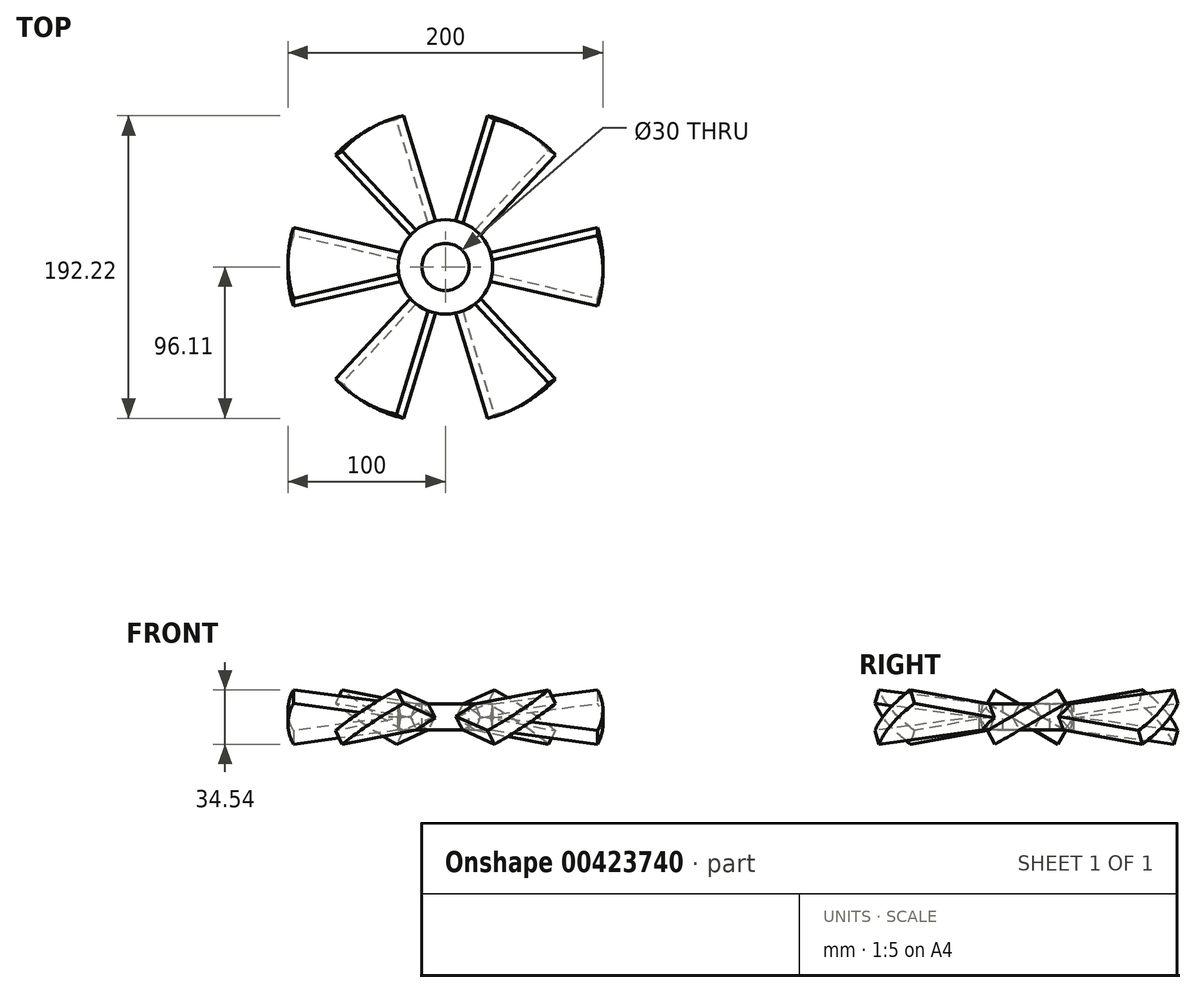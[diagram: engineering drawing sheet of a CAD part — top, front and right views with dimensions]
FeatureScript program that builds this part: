
annotation { "Feature Type Name" : "Feature", "Feature Type Description" : "" }
export const myFeature = defineFeature(function(context is Context, id is Id, definition is map)
    precondition{}
    {
        {
            var Q0;
            Q0=qCreatedBy(makeId("Top.planeOp"),FACE);
            var sketch = newSketch(context, id + "F0", { "sketchPlane" : qUnion([Q0])});
            skCircle(sketch, "E0", {"center": v(0, 0) * mm, "radius": 100 * mm});
            skCircle(sketch, "E1", {"center": v(0, 0) * mm, "radius": 30 * mm});
            skCircle(sketch, "E2", {"center": v(0, 0) * mm, "radius": 15 * mm});
            skLineSegment(sketch, "E3", {"start": v(0, 0) * mm, "end": v(15, 0) * mm});
            skLineSegment(sketch, "E4", {"start": v(14.49, 3.88) * mm, "end": v(96.6, 25.88) * mm});
            skLineSegment(sketch, "E5.MirrorCS", {"start": v(14.49, -3.88) * mm, "end": v(96.6, -25.88) * mm});
            skLineSegment(sketch, "E6", {"start": v(14.49, 3.88) * mm, "end": v(0, 0) * mm});
            skLineSegment(sketch, "E7", {"start": v(0, 0) * mm, "end": v(14.49, -3.88) * mm});
            skSolve(sketch);
        }
        {
            var Q0;
            {var subQ0=sQuery(id+"F0.wireOp",EDGE,"E4");var subQ1=sQuery(id+"F0.wireOp",EDGE,"E0");var subQ2=makeQuery(id+"F0.imprint","INTERSECT",VERTEX,{"derivedFrom":[subQ1,subQ0]});Q0=makeQuery(id+"F0.imprint","IMPRINT",FACE,{"disambiguationData":[TD([[makeQuery(id+"F0.imprint","IMPRINT",EDGE,{"disambiguationData":[TD([[subQ2,1.0]])],"derivedFrom":subQ1}),1.0]])]});}
            var Q1;
            {var subQ4=sQuery(id+"F0.wireOp",EDGE,"E4");var subQ6=sQuery(id+"F0.wireOp",EDGE,"E1");var subQ7=makeQuery(id+"F0.imprint","INTERSECT",VERTEX,{"derivedFrom":[subQ6,subQ4]});Q1=makeQuery(id+"F0.imprint","IMPRINT",FACE,{"disambiguationData":[TD([[makeQuery(id+"F0.imprint","IMPRINT",EDGE,{"disambiguationData":[TD([[subQ7,1.0]])],"derivedFrom":subQ6}),1.0]])]});}
            extrude(context, id + "F1", {"entities" : qUnion([Q0, Q1]), "endBound" : BoundingType.SYMMETRIC, "depth" : 10 * mm});
        }
        {
            var Q0;
            Q0=makeQuery(id+"F1.opExtrude","SWEPT_BODY",BODY,{"disambiguationData":[OSD([sQuery(id+"F0.wireOp",EDGE,"E0"),sQuery(id+"F0.wireOp",EDGE,"E2"),sQuery(id+"F0.wireOp",EDGE,"E4"),sQuery(id+"F0.wireOp",EDGE,"E5.MirrorCS")])]});
            var Q1;
            Q1=sQuery(id+"F0.wireOp",EDGE,"E3");
            var Q2;
            Q2=sQuery(id+"F0.wireOp",EDGE,"E3");
            transform(context, id + "F2", {"entities" : qUnion([Q0]), "transformType" : TransformType.ROTATION, "transformAxis" : qUnion([Q2]), "angle" : 30 * degree, "makeCopy" : false});
        }
        {
            var Q0;
            Q0=qCreatedBy(makeId("Front.planeOp"),FACE);
            var sketch = newSketch(context, id + "F3", { "sketchPlane" : qUnion([Q0])});
            skLineSegment(sketch, "E8", {"start": v(0, 0) * mm, "end": v(0, 34.54) * mm});
            skSolve(sketch);
        }
        {
            var Q0;
            Q0=makeQuery(id+"F1.opExtrude","SWEPT_BODY",BODY,{"disambiguationData":[OSD([sQuery(id+"F0.wireOp",EDGE,"E0"),sQuery(id+"F0.wireOp",EDGE,"E2"),sQuery(id+"F0.wireOp",EDGE,"E4"),sQuery(id+"F0.wireOp",EDGE,"E5.MirrorCS")])]});
            var Q1;
            Q1=sQuery(id+"F3.wireOp",EDGE,"E8");
            circularPattern(context, id + "F4", {"entities" : qUnion([Q0]), "axis" : qUnion([Q1]), "angle" : 360 * degree, "instanceCount" : 6, "equalSpace" : true});
        }
        {
            var Q0;
            {var subQ0=sQuery(id+"F0.wireOp",EDGE,"E4");var subQ1=sQuery(id+"F0.wireOp",EDGE,"E1");var subQ2=makeQuery(id+"F0.imprint","INTERSECT",VERTEX,{"derivedFrom":[subQ1,subQ0]});Q0=makeQuery(id+"F0.imprint","IMPRINT",FACE,{"disambiguationData":[TD([[makeQuery(id+"F0.imprint","IMPRINT",EDGE,{"disambiguationData":[TD([[subQ2,-1.0]])],"derivedFrom":subQ1}),1.0]])]});}
            var Q1;
            {var subQ0=sQuery(id+"F0.wireOp",EDGE,"E6");Q1=makeQuery(id+"F0.imprint","IMPRINT",FACE,{"disambiguationData":[TD([[makeQuery(id+"F0.imprint","IMPRINT",EDGE,{"derivedFrom":subQ0}),-1.0]])]});}
            var Q2;
            {var subQ0=sQuery(id+"F0.wireOp",EDGE,"E3");Q2=makeQuery(id+"F0.imprint","IMPRINT",FACE,{"disambiguationData":[TD([[makeQuery(id+"F0.imprint","IMPRINT",EDGE,{"derivedFrom":subQ0}),1.0]])]});}
            var Q3;
            {var subQ0=sQuery(id+"F0.wireOp",EDGE,"E3");Q3=makeQuery(id+"F0.imprint","IMPRINT",FACE,{"disambiguationData":[TD([[makeQuery(id+"F0.imprint","IMPRINT",EDGE,{"derivedFrom":subQ0}),-1.0]])]});}
            var Q4;
            {var subQ4=sQuery(id+"F0.wireOp",EDGE,"E4");var subQ6=sQuery(id+"F0.wireOp",EDGE,"E1");var subQ7=makeQuery(id+"F0.imprint","INTERSECT",VERTEX,{"derivedFrom":[subQ6,subQ4]});Q4=makeQuery(id+"F0.imprint","IMPRINT",FACE,{"disambiguationData":[TD([[makeQuery(id+"F0.imprint","IMPRINT",EDGE,{"disambiguationData":[TD([[subQ7,1.0]])],"derivedFrom":subQ6}),1.0]])]});}
            extrude(context, id + "F5", {"entities" : qUnion([Q0, Q1, Q2, Q3, Q4]), "operationType" : NewBodyOperationType.REMOVE, "endBound" : BoundingType.SYMMETRIC, "depth" : 25 * mm});
        }
        {
            var Q0;
            {var subQ0=sQuery(id+"F0.wireOp",EDGE,"E4");var subQ1=sQuery(id+"F0.wireOp",EDGE,"E1");var subQ2=makeQuery(id+"F0.imprint","INTERSECT",VERTEX,{"derivedFrom":[subQ1,subQ0]});Q0=makeQuery(id+"F0.imprint","IMPRINT",FACE,{"disambiguationData":[TD([[makeQuery(id+"F0.imprint","IMPRINT",EDGE,{"disambiguationData":[TD([[subQ2,-1.0]])],"derivedFrom":subQ1}),1.0]])]});}
            var Q1;
            {var subQ4=sQuery(id+"F0.wireOp",EDGE,"E4");var subQ6=sQuery(id+"F0.wireOp",EDGE,"E1");var subQ7=makeQuery(id+"F0.imprint","INTERSECT",VERTEX,{"derivedFrom":[subQ6,subQ4]});Q1=makeQuery(id+"F0.imprint","IMPRINT",FACE,{"disambiguationData":[TD([[makeQuery(id+"F0.imprint","IMPRINT",EDGE,{"disambiguationData":[TD([[subQ7,1.0]])],"derivedFrom":subQ6}),1.0]])]});}
            var Q2;
            {var subQ0=sQuery(id+"F0.wireOp",EDGE,"E5.MirrorCS");Q2=makeQuery(id+"F5.boolean.opBoolean","INTERSECT",VERTEX,{"derivedFrom":[makeQuery(id+"F4.opPattern","COPY",FACE,{"derivedFrom":makeQuery(id+"F1.opExtrude","CAP_FACE",FACE,{"disambiguationData":[OSD([sQuery(id+"F0.wireOp",EDGE,"E0"),sQuery(id+"F0.wireOp",EDGE,"E2"),sQuery(id+"F0.wireOp",EDGE,"E4"),subQ0])],"isStart":true}),"instanceName":"5"}),makeQuery(id+"F4.opPattern","COPY",FACE,{"derivedFrom":makeQuery(id+"F1.opExtrude","SWEPT_FACE",FACE,{"disambiguationData":[OSD([subQ0])]}),"instanceName":"5"}),makeQuery(id+"F5.opExtrude","SWEPT_FACE",FACE,{"disambiguationData":[OSD([sQuery(id+"F0.wireOp",EDGE,"E1")])]})]});}
            var Q3;
            {var subQ0=sQuery(id+"F0.wireOp",EDGE,"E4");Q3=makeQuery(id+"F5.boolean.opBoolean","INTERSECT",VERTEX,{"derivedFrom":[makeQuery(id+"F4.opPattern","COPY",FACE,{"derivedFrom":makeQuery(id+"F1.opExtrude","CAP_FACE",FACE,{"disambiguationData":[OSD([sQuery(id+"F0.wireOp",EDGE,"E0"),sQuery(id+"F0.wireOp",EDGE,"E2"),subQ0,sQuery(id+"F0.wireOp",EDGE,"E5.MirrorCS")])],"isStart":false}),"instanceName":"2"}),makeQuery(id+"F4.opPattern","COPY",FACE,{"derivedFrom":makeQuery(id+"F1.opExtrude","SWEPT_FACE",FACE,{"disambiguationData":[OSD([subQ0])]}),"instanceName":"2"}),makeQuery(id+"F5.opExtrude","SWEPT_FACE",FACE,{"disambiguationData":[OSD([sQuery(id+"F0.wireOp",EDGE,"E1")])]})]});}
            extrude(context, id + "F6", {"entities" : qUnion([Q0, Q1]), "endBound" : BoundingType.UP_TO_VERTEX, "oppositeDirection" : true, "endBoundEntityVertex" : qUnion([Q2]), "depth" : 25 * mm, "hasSecondDirection" : true, "secondDirectionBound" : SecondDirectionBoundingType.UP_TO_VERTEX, "secondDirectionOppositeDirection" : false, "secondDirectionBoundEntityVertex" : qUnion([Q3]), "secondDirectionDepth" : 25 * mm});
        }
    });
